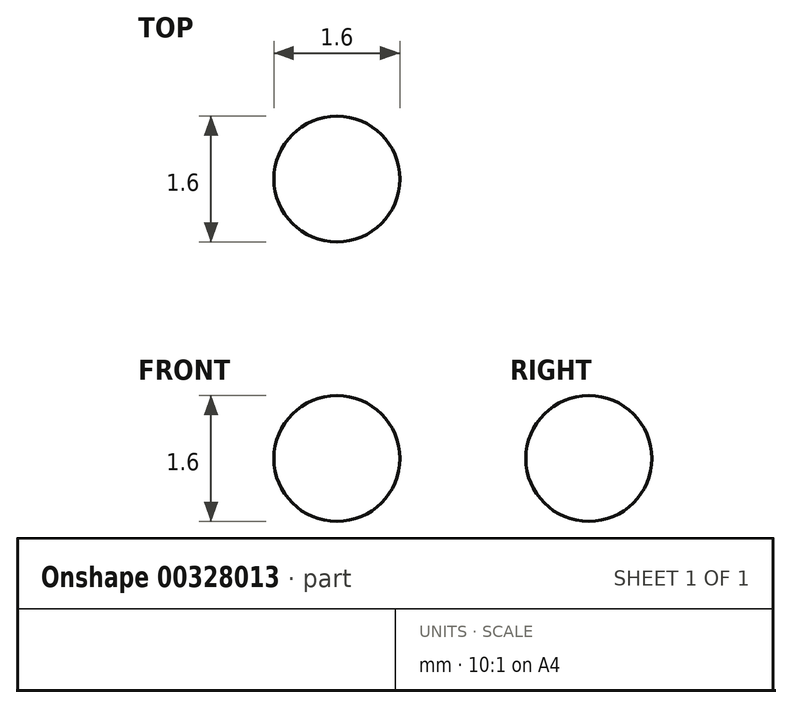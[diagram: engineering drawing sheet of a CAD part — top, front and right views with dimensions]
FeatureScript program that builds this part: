
annotation { "Feature Type Name" : "Feature", "Feature Type Description" : "" }
export const myFeature = defineFeature(function(context is Context, id is Id, definition is map)
    precondition{}
    {
        {
            var Q0;
            Q0=qCreatedBy(makeId("Front.planeOp"),FACE);
            var sketch = newSketch(context, id + "F0", { "sketchPlane" : qUnion([Q0])});
            skArc(sketch, "E0", {"start": v(0.8, 0) * mm, "mid": v(0, 0.8) * mm, "end": v(-0.8, 0) * mm});
            skLineSegment(sketch, "E1", {"start": v(-1.73, 0) * mm, "end": v(2.03, 0) * mm, "construction": true});
            skLineSegment(sketch, "E2", {"start": v(-0.8, 0) * mm, "end": v(0.8, 0) * mm});
            skSolve(sketch);
        }
        {
            var Q0;
            Q0 = qSketchRegion(id + "F0", true);
            var Q1;
            Q1=sQuery(id+"F0.wireOp",EDGE,"E1");
            revolve(context, id + "F1", {"entities" : qUnion([Q0]), "axis" : qUnion([Q1]), "revolveType" : RevolveType.FULL});
        }
    });
